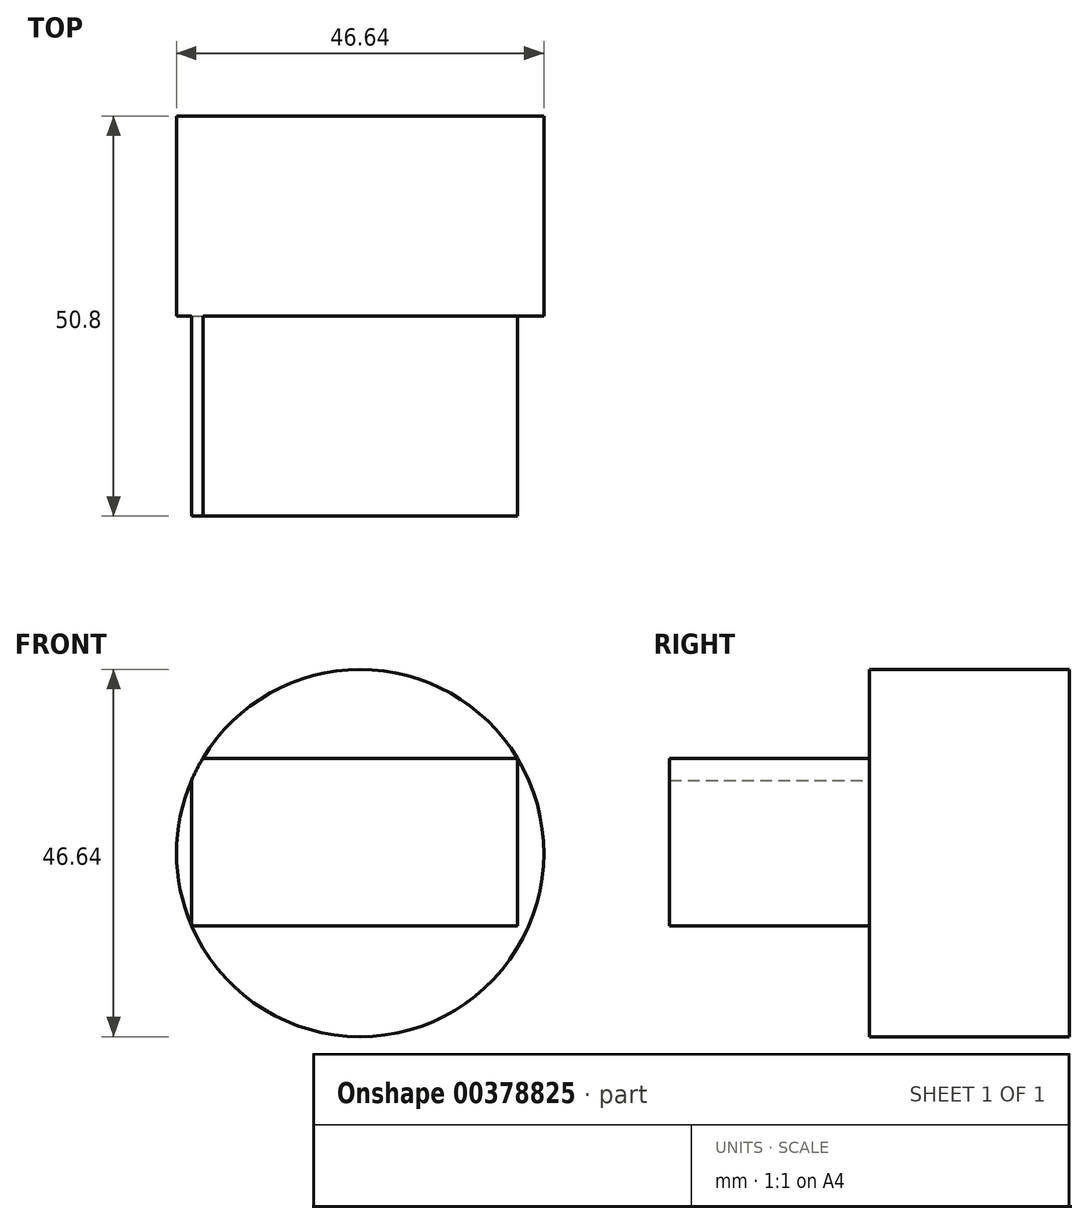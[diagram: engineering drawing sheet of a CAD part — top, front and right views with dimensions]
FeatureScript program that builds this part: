
annotation { "Feature Type Name" : "Feature", "Feature Type Description" : "" }
export const myFeature = defineFeature(function(context is Context, id is Id, definition is map)
    precondition{}
    {
        {
            var Q0;
            Q0=qCreatedBy(makeId("Front.planeOp"),FACE);
            var sketch = newSketch(context, id + "F0", { "sketchPlane" : qUnion([Q0])});
            skCircle(sketch, "E0", {"center": v(0, 0) * mm, "radius": 23.32 * mm});
            skSolve(sketch);
        }
        {
            var Q0;
            Q0=makeQuery(id+"F0.imprint","IMPRINT",FACE,{"disambiguationData":[TD([[makeQuery(id+"F0.imprint","IMPRINT",EDGE,{"derivedFrom":sQuery(id+"F0.wireOp",EDGE,"E0")}),1.0]])]});
            extrude(context, id + "F1", {"entities" : qUnion([Q0]), "depth" : 25.4 * mm});
        }
        {
            var Q0;
            Q0=makeQuery(id+"F1.opExtrude","CAP_FACE",FACE,{"disambiguationData":[OSD([sQuery(id+"F0.wireOp",EDGE,"E0")])],"isStart":false});
            var sketch = newSketch(context, id + "F2", { "sketchPlane" : qUnion([Q0])});
            skLineSegment(sketch, "E1.bottom", {"start": v(-21.42, -9.23) * mm, "end": v(19.97, -9.23) * mm});
            skLineSegment(sketch, "E1.top", {"start": v(-21.42, 12.04) * mm, "end": v(19.97, 12.04) * mm});
            skLineSegment(sketch, "E1.left", {"start": v(-21.42, -9.23) * mm, "end": v(-21.42, 12.04) * mm});
            skLineSegment(sketch, "E1.right", {"start": v(19.97, -9.23) * mm, "end": v(19.97, 12.04) * mm});
            skSolve(sketch);
        }
        {
            var Q0;
            {var subQ1=sQuery(id+"F2.wireOp",EDGE,"E1.bottom");Q0=makeQuery(id+"F2.imprint","IMPRINT",FACE,{"disambiguationData":[TD([[makeQuery(id+"F2.imprint","IMPRINT",EDGE,{"derivedFrom":subQ1}),1.0]])]});}
            extrude(context, id + "F3", {"entities" : qUnion([Q0]), "operationType" : NewBodyOperationType.ADD, "depth" : 25.4 * mm});
        }
    });
